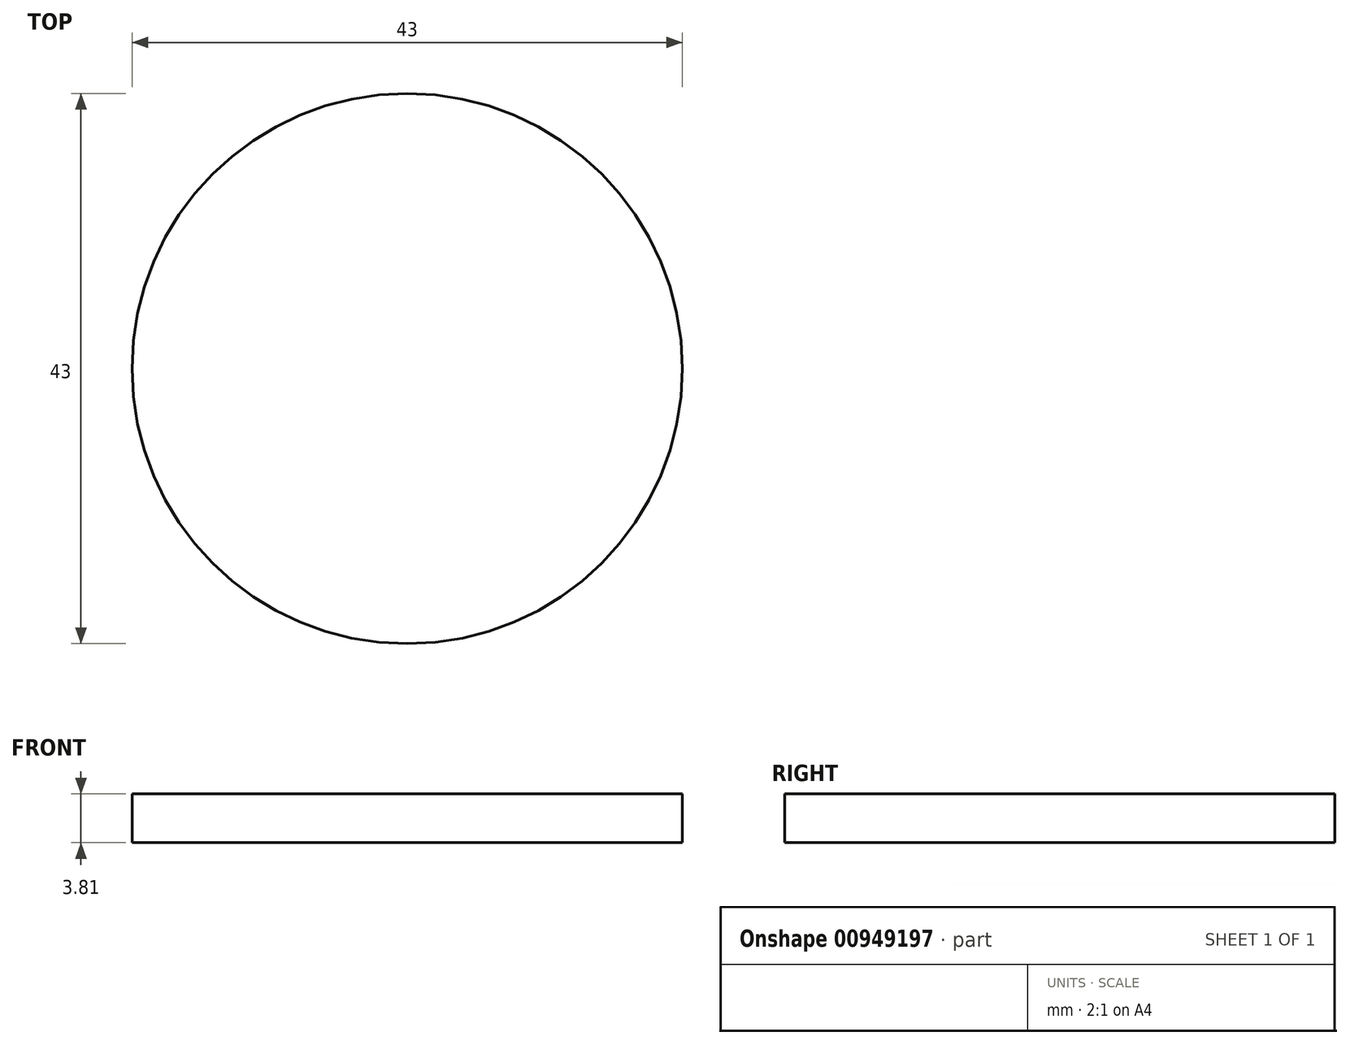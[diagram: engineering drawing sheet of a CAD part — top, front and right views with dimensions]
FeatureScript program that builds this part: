
annotation { "Feature Type Name" : "Feature", "Feature Type Description" : "" }
export const myFeature = defineFeature(function(context is Context, id is Id, definition is map)
    precondition{}
    {
        {
            var Q0;
            Q0=qCreatedBy(makeId("Top.planeOp"),FACE);
            var sketch = newSketch(context, id + "F0", { "sketchPlane" : qUnion([Q0])});
            skCircle(sketch, "E0", {"center": v(0, 0) * mm, "radius": 21.5 * mm});
            skSolve(sketch);
        }
        {
            var Q0;
            Q0=makeQuery(id+"F0.imprint","IMPRINT",FACE,{"disambiguationData":[TD([[makeQuery(id+"F0.imprint","IMPRINT",EDGE,{"derivedFrom":sQuery(id+"F0.wireOp",EDGE,"E0")}),1.0]])]});
            extrude(context, id + "F1", {"entities" : qUnion([Q0]), "depth" : 3.8 * mm, "offsetDistance" : 25.4 * mm});
        }
    });
